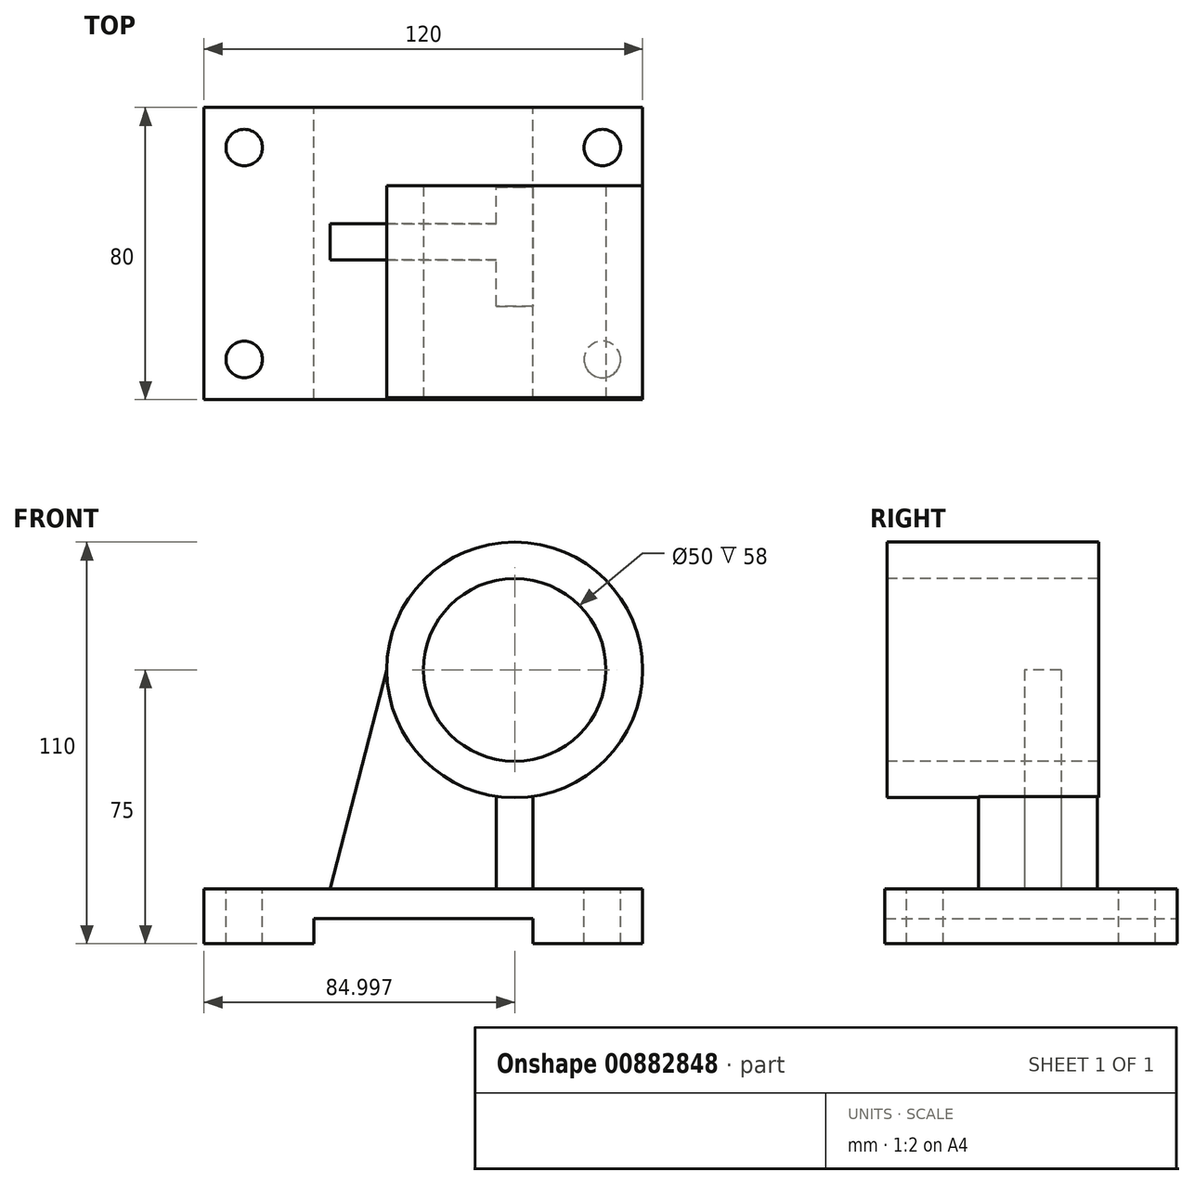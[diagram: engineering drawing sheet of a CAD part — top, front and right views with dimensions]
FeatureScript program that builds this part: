
annotation { "Feature Type Name" : "Feature", "Feature Type Description" : "" }
export const myFeature = defineFeature(function(context is Context, id is Id, definition is map)
    precondition{}
    {
        {
            var Q0;
            Q0=qCreatedBy(makeId("Front.planeOp"),FACE);
            var sketch = newSketch(context, id + "F0", { "sketchPlane" : qUnion([Q0])});
            skLineSegment(sketch, "E0", {"start": v(-36.51, 0) * mm, "end": v(-66.51, 0) * mm});
            skLineSegment(sketch, "E1", {"start": v(-66.51, 0) * mm, "end": v(-66.51, 15) * mm});
            skLineSegment(sketch, "E2", {"start": v(-66.51, 15) * mm, "end": v(53.49, 15) * mm});
            skLineSegment(sketch, "E3", {"start": v(53.49, 15) * mm, "end": v(53.49, 0) * mm});
            skLineSegment(sketch, "E4", {"start": v(53.49, 0) * mm, "end": v(23.49, 0) * mm});
            skLineSegment(sketch, "E5", {"start": v(-36.51, 0) * mm, "end": v(-36.51, 6.96) * mm});
            skLineSegment(sketch, "E6", {"start": v(-36.51, 6.96) * mm, "end": v(23.49, 6.96) * mm});
            skLineSegment(sketch, "E7", {"start": v(23.49, 0) * mm, "end": v(23.49, 6.96) * mm});
            skSolve(sketch);
        }
        {
            var Q0;
            Q0 = qSketchRegion(id + "F0", true);
            extrude(context, id + "F1", {"entities" : qUnion([Q0]), "depth" : 80 * mm, "offsetDistance" : 25 * mm});
        }
        {
            var Q0;
            Q0=makeQuery(id+"F1.opExtrude","SWEPT_FACE",FACE,{"disambiguationData":[OSD([sQuery(id+"F0.wireOp",EDGE,"E2")])]});
            var sketch = newSketch(context, id + "F2", { "sketchPlane" : qUnion([Q0])});
            skCircle(sketch, "E8", {"center": v(-55.51, -11) * mm, "radius": 5 * mm});
            skCircle(sketch, "E9", {"center": v(42.49, -11) * mm, "radius": 5 * mm});
            skCircle(sketch, "E10", {"center": v(42.49, -69) * mm, "radius": 5 * mm});
            skCircle(sketch, "E11", {"center": v(-55.51, -69) * mm, "radius": 5 * mm});
            skSolve(sketch);
        }
        {
            var Q0;
            Q0=makeQuery(id+"F2.imprint","IMPRINT",FACE,{"disambiguationData":[TD([[makeQuery(id+"F2.imprint","IMPRINT",EDGE,{"derivedFrom":sQuery(id+"F2.wireOp",EDGE,"E9")}),1.0]])]});
            var Q1;
            Q1=makeQuery(id+"F2.imprint","IMPRINT",FACE,{"disambiguationData":[TD([[makeQuery(id+"F2.imprint","IMPRINT",EDGE,{"derivedFrom":sQuery(id+"F2.wireOp",EDGE,"E10")}),1.0]])]});
            var Q2;
            Q2=makeQuery(id+"F2.imprint","IMPRINT",FACE,{"disambiguationData":[TD([[makeQuery(id+"F2.imprint","IMPRINT",EDGE,{"derivedFrom":sQuery(id+"F2.wireOp",EDGE,"E11")}),1.0]])]});
            var Q3;
            Q3=makeQuery(id+"F2.imprint","IMPRINT",FACE,{"disambiguationData":[TD([[makeQuery(id+"F2.imprint","IMPRINT",EDGE,{"derivedFrom":sQuery(id+"F2.wireOp",EDGE,"E8")}),1.0]])]});
            extrude(context, id + "F3", {"entities" : qUnion([Q0, Q1, Q2, Q3]), "operationType" : NewBodyOperationType.REMOVE, "oppositeDirection" : true, "depth" : 25 * mm, "offsetDistance" : 25 * mm});
        }
        {
            var Q0;
            Q0=makeQuery(id+"F1.opExtrude","SWEPT_FACE",FACE,{"disambiguationData":[OSD([sQuery(id+"F0.wireOp",EDGE,"E2")])]});
            var sketch = newSketch(context, id + "F4", { "sketchPlane" : qUnion([Q0])});
            skLineSegment(sketch, "E12", {"start": v(23.49, -21.8) * mm, "end": v(23.49, -54.41) * mm});
            skLineSegment(sketch, "E13", {"start": v(23.49, -54.41) * mm, "end": v(13.49, -54.41) * mm});
            skLineSegment(sketch, "E14", {"start": v(13.49, -54.41) * mm, "end": v(13.49, -41.8) * mm});
            skLineSegment(sketch, "E15", {"start": v(13.49, -31.8) * mm, "end": v(13.49, -21.8) * mm});
            skLineSegment(sketch, "E16", {"start": v(23.49, -21.8) * mm, "end": v(13.49, -21.8) * mm});
            skLineSegment(sketch, "E17", {"start": v(13.49, -31.8) * mm, "end": v(-32.01, -31.8) * mm});
            skLineSegment(sketch, "E18", {"start": v(13.49, -41.8) * mm, "end": v(-32.01, -41.8) * mm});
            skLineSegment(sketch, "E19", {"start": v(-32.01, -31.8) * mm, "end": v(-32.01, -41.8) * mm});
            skSolve(sketch);
        }
        {
            var Q0;
            Q0 = qSketchRegion(id + "F4", true);
            extrude(context, id + "F5", {"entities" : qUnion([Q0]), "operationType" : NewBodyOperationType.ADD, "depth" : 60 * mm, "offsetDistance" : 25 * mm});
        }
        {
            var Q0;
            Q0=makeQuery(id+"F5.opExtrude","SWEPT_FACE",FACE,{"disambiguationData":[OSD([sQuery(id+"F4.wireOp",EDGE,"E13")])]});
            var sketch = newSketch(context, id + "F6", { "sketchPlane" : qUnion([Q0])});
            skCircle(sketch, "E20", {"center": v(18.49, 75) * mm, "radius": 35 * mm});
            skSolve(sketch);
        }
        {
            var Q0;
            Q0 = qSketchRegion(id + "F6", true);
            extrude(context, id + "F7", {"entities" : qUnion([Q0]), "operationType" : NewBodyOperationType.ADD, "oppositeDirection" : true, "depth" : 33 * mm, "offsetDistance" : 25 * mm});
        }
        {
            var Q0;
            Q0 = qSketchRegion(id + "F6", true);
            extrude(context, id + "F8", {"entities" : qUnion([Q0]), "operationType" : NewBodyOperationType.ADD, "depth" : 25 * mm, "offsetDistance" : 25 * mm});
        }
        {
            var Q0;
            Q0=makeQuery(id+"F8.opExtrude","CAP_FACE",FACE,{"disambiguationData":[OSD([sQuery(id+"F6.wireOp",EDGE,"E20")])],"isStart":false});
            var sketch = newSketch(context, id + "F9", { "sketchPlane" : qUnion([Q0])});
            skCircle(sketch, "E21", {"center": v(18.49, 75) * mm, "radius": 25 * mm});
            skSolve(sketch);
        }
        {
            var Q0;
            Q0=makeQuery(id+"F9.imprint","IMPRINT",FACE,{"disambiguationData":[TD([[makeQuery(id+"F9.imprint","IMPRINT",EDGE,{"derivedFrom":sQuery(id+"F9.wireOp",EDGE,"E21")}),1.0]])]});
            extrude(context, id + "F10", {"entities" : qUnion([Q0]), "operationType" : NewBodyOperationType.REMOVE, "oppositeDirection" : true, "depth" : 52.6 * mm, "offsetDistance" : 25 * mm});
        }
        {
            var Q0;
            Q0=makeQuery(id+"F7.opExtrude","CAP_FACE",FACE,{"disambiguationData":[OSD([sQuery(id+"F6.wireOp",EDGE,"E20")])],"isStart":false});
            var sketch = newSketch(context, id + "F11", { "sketchPlane" : qUnion([Q0])});
            skCircle(sketch, "E22", {"center": v(-18.49, 75) * mm, "radius": 25 * mm});
            skSolve(sketch);
        }
        {
            var Q0;
            Q0 = qSketchRegion(id + "F11", true);
            extrude(context, id + "F12", {"entities" : qUnion([Q0]), "operationType" : NewBodyOperationType.REMOVE, "oppositeDirection" : true, "depth" : 52.6 * mm, "offsetDistance" : 25 * mm});
        }
        {
            var Q0;
            Q0=makeQuery(id+"F5.opExtrude","SWEPT_FACE",FACE,{"disambiguationData":[OSD([sQuery(id+"F4.wireOp",EDGE,"E18")])]});
            var sketch = newSketch(context, id + "F13", { "sketchPlane" : qUnion([Q0])});
            skLineSegment(sketch, "E23", {"start": v(-16.51, 75) * mm, "end": v(-32.01, 75) * mm});
            skLineSegment(sketch, "E24", {"start": v(-32.01, 75) * mm, "end": v(-32.01, 15) * mm});
            skLineSegment(sketch, "E25", {"start": v(-16.51, 75) * mm, "end": v(-32.01, 15) * mm});
            skSolve(sketch);
        }
        {
            var Q0;
            Q0 = qSketchRegion(id + "F13", true);
            extrude(context, id + "F14", {"entities" : qUnion([Q0]), "operationType" : NewBodyOperationType.REMOVE, "oppositeDirection" : true, "depth" : 25 * mm, "offsetDistance" : 25 * mm});
        }
    });
